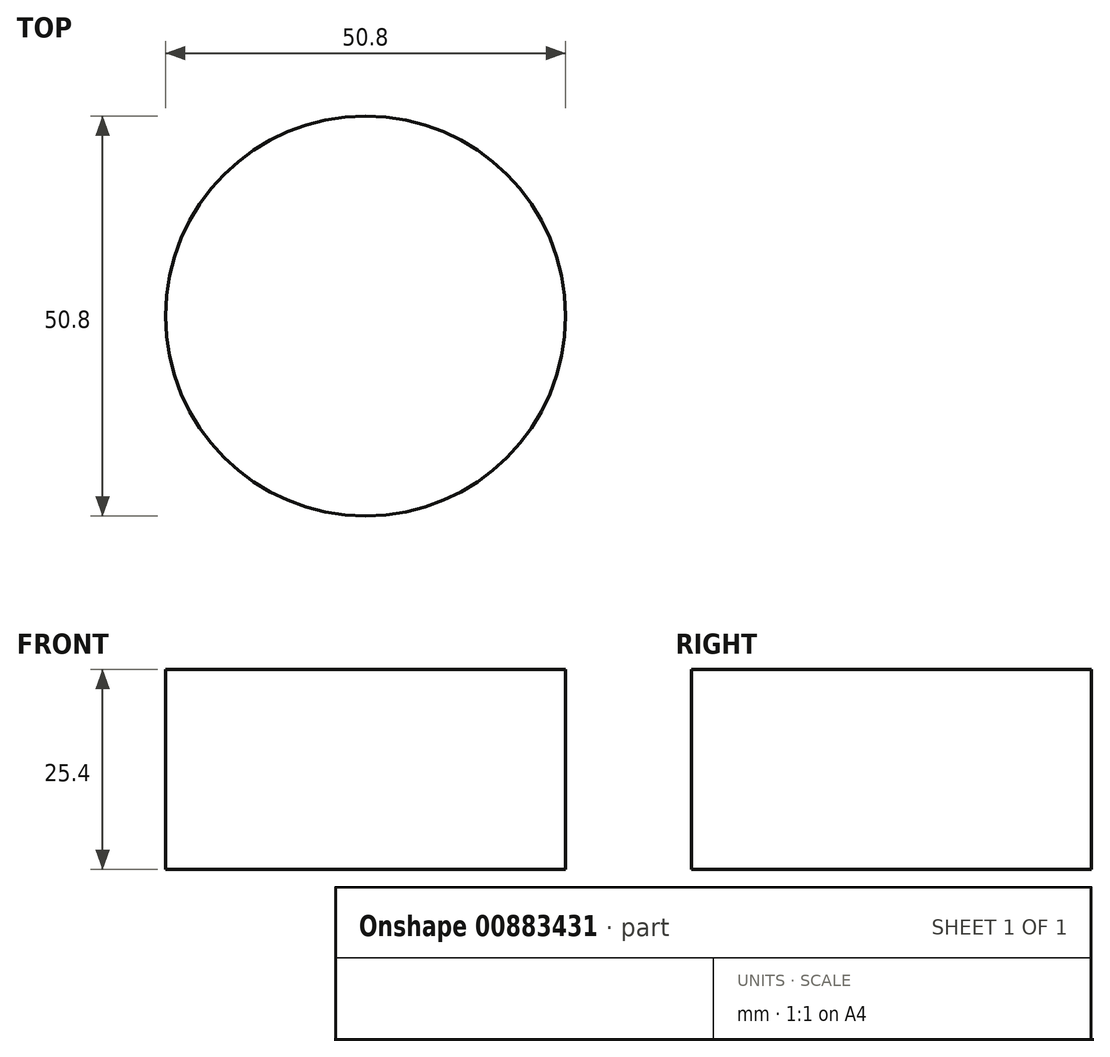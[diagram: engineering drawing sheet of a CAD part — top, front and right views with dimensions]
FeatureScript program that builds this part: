
annotation { "Feature Type Name" : "Feature", "Feature Type Description" : "" }
export const myFeature = defineFeature(function(context is Context, id is Id, definition is map)
    precondition{}
    {
        {
            var Q0;
            Q0=qCreatedBy(makeId("Top.planeOp"),FACE);
            var sketch = newSketch(context, id + "F0", { "sketchPlane" : qUnion([Q0])});
            skCircle(sketch, "E0", {"center": v(-28.78, 50.92) * mm, "radius": 25.4 * mm});
            skSolve(sketch);
        }
        {
            var Q0;
            Q0 = qSketchRegion(id + "F0", true);
            extrude(context, id + "F1", {"entities" : qUnion([Q0]), "depth" : 25.4 * mm, "offsetDistance" : 25.4 * mm});
        }
    });
